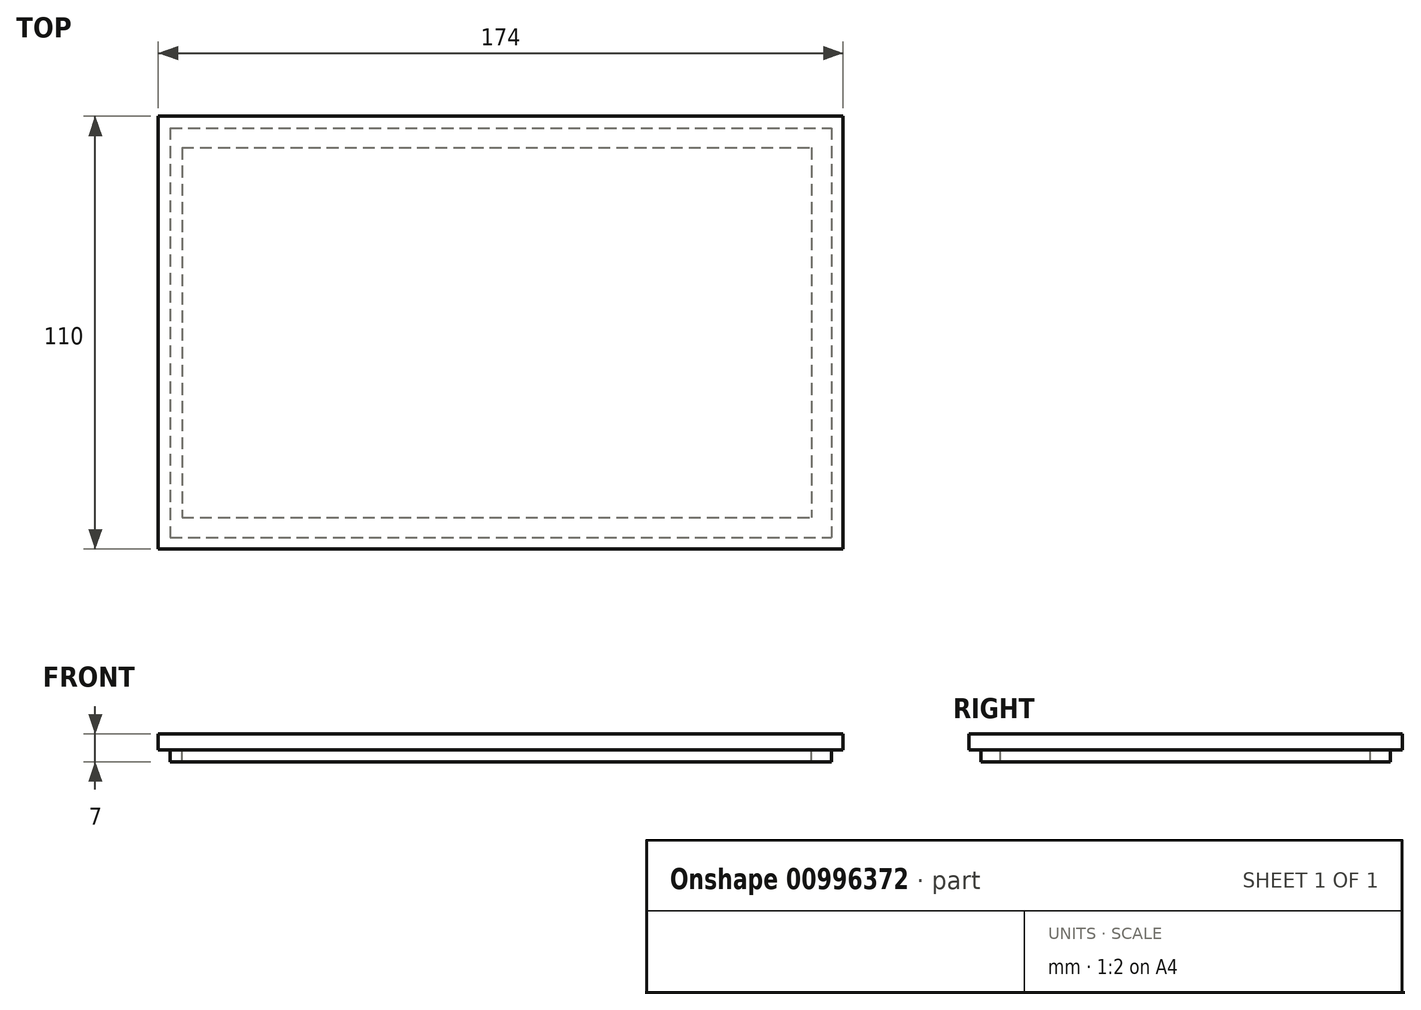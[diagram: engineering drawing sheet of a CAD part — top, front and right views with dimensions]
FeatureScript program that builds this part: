
annotation { "Feature Type Name" : "Feature", "Feature Type Description" : "" }
export const myFeature = defineFeature(function(context is Context, id is Id, definition is map)
    precondition{}
    {
        {
            var Q0;
            Q0=qCreatedBy(makeId("Top.planeOp"),FACE);
            var sketch = newSketch(context, id + "F0", { "sketchPlane" : qUnion([Q0])});
            skLineSegment(sketch, "E0.bottom", {"start": v(-87, 55) * mm, "end": v(87, 55) * mm});
            skLineSegment(sketch, "E0.top", {"start": v(-87, -55) * mm, "end": v(87, -55) * mm});
            skLineSegment(sketch, "E0.left", {"start": v(-87, 55) * mm, "end": v(-87, -55) * mm});
            skLineSegment(sketch, "E0.right", {"start": v(87, 55) * mm, "end": v(87, -55) * mm});
            skPoint(sketch, "E0.middle", {"position": v(0, 0) * mm});
            skSolve(sketch);
        }
        {
            var Q0;
            Q0 = qSketchRegion(id + "F0", true);
            extrude(context, id + "F1", {"entities" : qUnion([Q0]), "depth" : 4 * mm, "offsetDistance" : 25 * mm});
        }
        {
            var Q0;
            Q0=makeQuery(id+"F1.opExtrude","CAP_FACE",FACE,{"disambiguationData":[OSD([sQuery(id+"F0.wireOp",EDGE,"E0.bottom"),sQuery(id+"F0.wireOp",EDGE,"E0.top"),sQuery(id+"F0.wireOp",EDGE,"E0.left"),sQuery(id+"F0.wireOp",EDGE,"E0.right")])],"isStart":true});
            var sketch = newSketch(context, id + "F2", { "sketchPlane" : qUnion([Q0])});
            skLineSegment(sketch, "E1.0", {"start": v(-84, -52) * mm, "end": v(-84, 52) * mm});
            skLineSegment(sketch, "E1.1", {"start": v(-84, -52) * mm, "end": v(84, -52) * mm});
            skLineSegment(sketch, "E1.2", {"start": v(84, -52) * mm, "end": v(84, 52) * mm});
            skLineSegment(sketch, "E1.3", {"start": v(-84, 52) * mm, "end": v(84, 52) * mm});
            skLineSegment(sketch, "E2.0", {"start": v(-81, -52) * mm, "end": v(-81, 52) * mm});
            skLineSegment(sketch, "E3.0", {"start": v(-84, -47) * mm, "end": v(79, -47) * mm});
            skLineSegment(sketch, "E3.1", {"start": v(79, -47) * mm, "end": v(79, 47) * mm});
            skLineSegment(sketch, "E3.2", {"start": v(-84, 47) * mm, "end": v(79, 47) * mm});
            skSolve(sketch);
        }
        {
            var Q0;
            {var subQ0=sQuery(id+"F2.wireOp",EDGE,"E1.1");var subQ1=sQuery(id+"F2.wireOp",EDGE,"E1.0");var subQ2=makeQuery(id+"F2.imprint","INTERSECT",VERTEX,{"derivedFrom":[subQ1,subQ0]});Q0=makeQuery(id+"F2.imprint","IMPRINT",FACE,{"disambiguationData":[TD([[makeQuery(id+"F2.imprint","IMPRINT",EDGE,{"disambiguationData":[TD([[subQ2,-1.0]])],"derivedFrom":subQ1}),-1.0]])]});}
            var Q1;
            {var subQ6=sQuery(id+"F2.wireOp",EDGE,"E1.2");Q1=makeQuery(id+"F2.imprint","IMPRINT",FACE,{"disambiguationData":[TD([[makeQuery(id+"F2.imprint","IMPRINT",EDGE,{"derivedFrom":subQ6}),1.0]])]});}
            var Q2;
            {var subQ0=sQuery(id+"F2.wireOp",EDGE,"E3.0");var subQ1=sQuery(id+"F2.wireOp",EDGE,"E1.0");var subQ2=makeQuery(id+"F2.imprint","INTERSECT",VERTEX,{"derivedFrom":[subQ1,subQ0]});Q2=makeQuery(id+"F2.imprint","IMPRINT",FACE,{"disambiguationData":[TD([[makeQuery(id+"F2.imprint","IMPRINT",EDGE,{"disambiguationData":[TD([[subQ2,-1.0]])],"derivedFrom":subQ1}),-1.0]])]});}
            var Q3;
            {var subQ0=sQuery(id+"F2.wireOp",EDGE,"E1.3");var subQ1=sQuery(id+"F2.wireOp",EDGE,"E1.0");var subQ2=makeQuery(id+"F2.imprint","INTERSECT",VERTEX,{"derivedFrom":[subQ1,subQ0]});Q3=makeQuery(id+"F2.imprint","IMPRINT",FACE,{"disambiguationData":[TD([[makeQuery(id+"F2.imprint","IMPRINT",EDGE,{"disambiguationData":[TD([[subQ2,1.0]])],"derivedFrom":subQ1}),-1.0]])]});}
            extrude(context, id + "F3", {"entities" : qUnion([Q0, Q1, Q2, Q3]), "operationType" : NewBodyOperationType.ADD, "depth" : 3 * mm, "offsetDistance" : 25 * mm});
        }
    });
